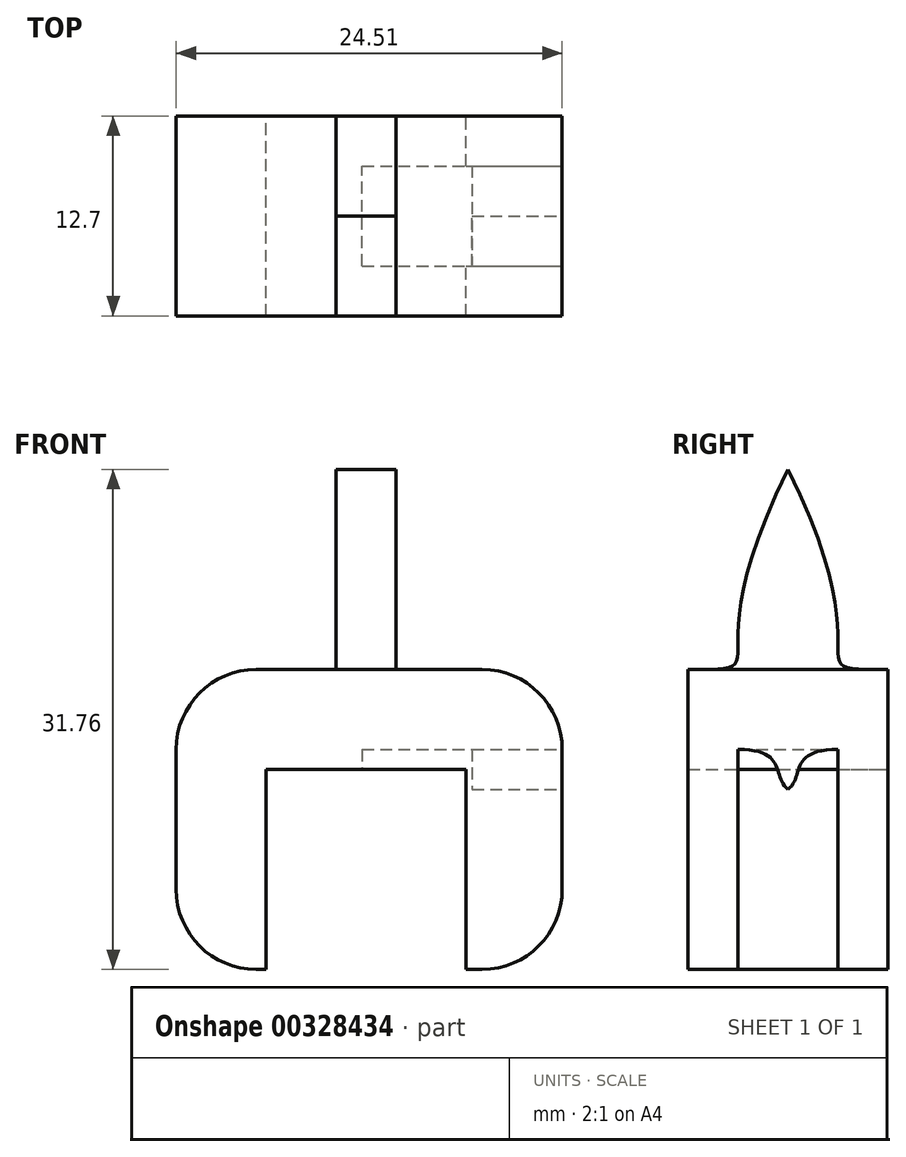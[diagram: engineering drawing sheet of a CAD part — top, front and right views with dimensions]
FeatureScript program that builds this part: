
annotation { "Feature Type Name" : "Feature", "Feature Type Description" : "" }
export const myFeature = defineFeature(function(context is Context, id is Id, definition is map)
    precondition{}
    {
        {
            var Q0;
            Q0=qCreatedBy(makeId("Front.planeOp"),FACE);
            var sketch = newSketch(context, id + "F0", { "sketchPlane" : qUnion([Q0])});
            skLineSegment(sketch, "E0.bottom", {"start": v(-6.35, 3.17) * mm, "end": v(6.35, 3.17) * mm});
            skLineSegment(sketch, "E0.top", {"start": v(-6.35, -3.18) * mm, "end": v(6.35, -3.18) * mm});
            skLineSegment(sketch, "E0.left", {"start": v(-6.35, 3.17) * mm, "end": v(-6.35, -3.18) * mm});
            skLineSegment(sketch, "E0.right", {"start": v(6.35, 3.18) * mm, "end": v(6.35, -3.18) * mm});
            skPoint(sketch, "E0.middle", {"position": v(0, 0) * mm});
            skLineSegment(sketch, "E1.bottom", {"start": v(-6.35, 3.17) * mm, "end": v(-12.05, 3.17) * mm});
            skLineSegment(sketch, "E1.top", {"start": v(-6.35, -15.88) * mm, "end": v(-12.05, -15.88) * mm});
            skLineSegment(sketch, "E1.left", {"start": v(-6.35, 3.17) * mm, "end": v(-6.35, -15.88) * mm});
            skLineSegment(sketch, "E1.right", {"start": v(-12.05, 3.17) * mm, "end": v(-12.05, -15.88) * mm});
            skLineSegment(sketch, "E2.bottom", {"start": v(6.35, 3.17) * mm, "end": v(12.46, 3.17) * mm});
            skLineSegment(sketch, "E2.top", {"start": v(6.35, -15.88) * mm, "end": v(12.46, -15.88) * mm});
            skLineSegment(sketch, "E2.left", {"start": v(6.35, 3.17) * mm, "end": v(6.35, -15.88) * mm});
            skLineSegment(sketch, "E2.right", {"start": v(12.46, 3.17) * mm, "end": v(12.46, -15.88) * mm});
            skSolve(sketch);
        }
        {
            var Q0;
            {var subQ3=sQuery(id+"F0.wireOp",EDGE,"E1.bottom");Q0=makeQuery(id+"F0.imprint","IMPRINT",FACE,{"disambiguationData":[TD([[makeQuery(id+"F0.imprint","IMPRINT",EDGE,{"derivedFrom":subQ3}),1.0]])]});}
            var Q1;
            {var subQ0=sQuery(id+"F0.wireOp",EDGE,"E0.bottom");Q1=makeQuery(id+"F0.imprint","IMPRINT",FACE,{"disambiguationData":[TD([[makeQuery(id+"F0.imprint","IMPRINT",EDGE,{"derivedFrom":subQ0}),-1.0]])]});}
            var Q2;
            {var subQ3=sQuery(id+"F0.wireOp",EDGE,"E2.bottom");Q2=makeQuery(id+"F0.imprint","IMPRINT",FACE,{"disambiguationData":[TD([[makeQuery(id+"F0.imprint","IMPRINT",EDGE,{"derivedFrom":subQ3}),-1.0]])]});}
            extrude(context, id + "F1", {"entities" : qUnion([Q0, Q1, Q2]), "depth" : 12.7 * mm});
        }
        {
            var Q0;
            Q0=makeQuery(id+"F1.opExtrude","SWEPT_EDGE",EDGE,{"disambiguationData":[OSD([sQuery(id+"F0.wireOp",EDGE,"E1.bottom"),sQuery(id+"F0.wireOp",EDGE,"E1.right")])]});
            var Q1;
            Q1=makeQuery(id+"F1.opExtrude","SWEPT_EDGE",EDGE,{"disambiguationData":[OSD([sQuery(id+"F0.wireOp",EDGE,"E2.bottom"),sQuery(id+"F0.wireOp",EDGE,"E2.right")])]});
            var Q2;
            Q2=makeQuery(id+"F1.opExtrude","SWEPT_EDGE",EDGE,{"disambiguationData":[OSD([sQuery(id+"F0.wireOp",EDGE,"E1.top"),sQuery(id+"F0.wireOp",EDGE,"E1.right")])]});
            var Q3;
            Q3=makeQuery(id+"F1.opExtrude","SWEPT_EDGE",EDGE,{"disambiguationData":[OSD([sQuery(id+"F0.wireOp",EDGE,"E2.top"),sQuery(id+"F0.wireOp",EDGE,"E2.right")])]});
            fillet(context, id + "F2", {"entities" : qUnion([Q0, Q1, Q2, Q3]), "radius" : 5.08 * mm, "tangentPropagation" : true, "allowEdgeOverflow" : false});
        }
        {
            var Q0;
            Q0=makeQuery(id+"F1.opExtrude","SWEPT_FACE",FACE,{"disambiguationData":[OSD([sQuery(id+"F0.wireOp",EDGE,"E2.right")])]});
            var sketch = newSketch(context, id + "F3", { "sketchPlane" : qUnion([Q0])});
            skLineSegment(sketch, "E3.bottom", {"start": v(-9.53, -1.9) * mm, "end": v(-3.18, -1.9) * mm});
            skLineSegment(sketch, "E3.top", {"start": v(-9.53, -19.68) * mm, "end": v(-3.18, -19.68) * mm});
            skLineSegment(sketch, "E3.left", {"start": v(-9.53, -1.9) * mm, "end": v(-9.53, -19.68) * mm});
            skLineSegment(sketch, "E3.right", {"start": v(-3.18, -1.9) * mm, "end": v(-3.18, -19.68) * mm});
            skPoint(sketch, "E3.middle", {"position": v(-6.35, -10.8) * mm});
            skSolve(sketch);
        }
        {
            var Q0;
            {var subQ0=sQuery(id+"F3.wireOp",EDGE,"E3.bottom");Q0=makeQuery(id+"F3.imprint","IMPRINT",FACE,{"disambiguationData":[TD([[makeQuery(id+"F3.imprint","IMPRINT",EDGE,{"derivedFrom":subQ0}),1.0]])]});}
            var Q1;
            {var subQ0=sQuery(id+"F3.wireOp",EDGE,"E3.top");Q1=makeQuery(id+"F3.imprint","IMPRINT",FACE,{"disambiguationData":[TD([[makeQuery(id+"F3.imprint","IMPRINT",EDGE,{"derivedFrom":subQ0}),1.0]])]});}
            extrude(context, id + "F4", {"entities" : qUnion([Q0, Q1]), "operationType" : NewBodyOperationType.REMOVE, "oppositeDirection" : true, "depth" : 12.7 * mm});
        }
        {
            var Q0;
            {var subQ0=sQuery(id+"F0.wireOp",EDGE,"E2.right");Q0=makeQuery(id+"F4.boolean.opBoolean","SPLIT",FACE,{"disambiguationData":[TD([makeQuery(id+"F4.opExtrude","SWEPT_FACE",FACE,{"disambiguationData":[OSD([sQuery(id+"F3.wireOp",EDGE,"E3.left")])]})])],"derivedFrom":makeQuery(id+"F1.opExtrude","SWEPT_FACE",FACE,{"disambiguationData":[OSD([subQ0])]})});}
            var sketch = newSketch(context, id + "F5", { "sketchPlane" : qUnion([Q0])});
            skPoint(sketch, "E4", {"position": v(-6.35, -1.9) * mm});
            skLineSegment(sketch, "E5", {"start": v(-3.17, -1.9) * mm, "end": v(-9.53, -1.9) * mm});
            skLineSegment(sketch, "E6", {"start": v(-6.35, -1.9) * mm, "end": v(-6.35, -4.45) * mm});
            skFitSpline(sketch, "E7", {"points": [v(-9.53, -1.9) * mm, v(-6.35, -4.45) * mm], "startDerivative": vector(9.53, 0) * mm, "endDerivative": vector(3.17, -2.54) * mm});
            skFitSpline(sketch, "E8", {"points": [v(-3.17, -1.9) * mm, v(-6.35, -4.45) * mm], "startDerivative": vector(-9.53, 0) * mm, "endDerivative": vector(-3.18, -2.54) * mm});
            skSolve(sketch);
        }
        {
            var Q0;
            {var subQ6=sQuery(id+"F5.wireOp",EDGE,"E6");Q0=makeQuery(id+"F5.imprint","IMPRINT",FACE,{"disambiguationData":[TD([[makeQuery(id+"F5.imprint","IMPRINT",EDGE,{"derivedFrom":subQ6}),-1.0]])]});}
            var Q1;
            {var subQ2=sQuery(id+"F5.wireOp",EDGE,"E6");Q1=makeQuery(id+"F5.imprint","IMPRINT",FACE,{"disambiguationData":[TD([[makeQuery(id+"F5.imprint","IMPRINT",EDGE,{"derivedFrom":subQ2}),1.0]])]});}
            extrude(context, id + "F6", {"entities" : qUnion([Q0, Q1]), "operationType" : NewBodyOperationType.ADD, "oppositeDirection" : true, "depth" : 5.7 * mm});
        }
        {
            var Q0;
            Q0=makeQuery(id+"F1.opExtrude","SWEPT_FACE",FACE,{"disambiguationData":[OSD([sQuery(id+"F0.wireOp",EDGE,"E0.bottom"),sQuery(id+"F0.wireOp",EDGE,"E1.bottom"),sQuery(id+"F0.wireOp",EDGE,"E2.bottom")])]});
            var sketch = newSketch(context, id + "F7", { "sketchPlane" : qUnion([Q0])});
            skLineSegment(sketch, "E9.bottom", {"start": v(-1.9, 0) * mm, "end": v(1.9, 0) * mm});
            skLineSegment(sketch, "E9.top", {"start": v(-1.9, -12.7) * mm, "end": v(1.9, -12.7) * mm});
            skLineSegment(sketch, "E9.left", {"start": v(-1.9, 0) * mm, "end": v(-1.9, -12.7) * mm});
            skLineSegment(sketch, "E9.right", {"start": v(1.9, 0) * mm, "end": v(1.9, -12.7) * mm});
            skSolve(sketch);
        }
        {
            var Q0;
            Q0=makeQuery(id+"F7.imprint","IMPRINT",FACE,{"disambiguationData":[TD([[makeQuery(id+"F7.imprint","IMPRINT",EDGE,{"derivedFrom":sQuery(id+"F7.wireOp",EDGE,"E9.bottom")}),1.0]])]});
            extrude(context, id + "F8", {"entities" : qUnion([Q0]), "operationType" : NewBodyOperationType.ADD, "depth" : 12.7 * mm});
        }
        {
            var Q0;
            Q0=makeQuery(id+"F8.opExtrude","SWEPT_FACE",FACE,{"disambiguationData":[OSD([sQuery(id+"F7.wireOp",EDGE,"E9.right")])]});
            var sketch = newSketch(context, id + "F9", { "sketchPlane" : qUnion([Q0])});
            skPoint(sketch, "E10", {"position": v(-6.35, 15.88) * mm});
            skFitSpline(sketch, "E11", {"points": [v(-12.7, 3.17) * mm, v(-6.35, 15.88) * mm], "startDerivative": vector(19.05, 0) * mm, "endDerivative": vector(19.05, 38.1) * mm});
            skFitSpline(sketch, "E12", {"points": [v(-6.35, 15.88) * mm, v(0, 3.17) * mm], "startDerivative": vector(19.05, -38.1) * mm, "endDerivative": vector(19.05, 0) * mm});
            skSolve(sketch);
        }
        {
            var Q0;
            {var subQ0=sQuery(id+"F9.wireOp",EDGE,"E11");Q0=makeQuery(id+"F9.imprint","IMPRINT",FACE,{"disambiguationData":[TD([[makeQuery(id+"F9.imprint","IMPRINT",EDGE,{"derivedFrom":subQ0}),1.0]])]});}
            var Q1;
            {var subQ0=sQuery(id+"F9.wireOp",EDGE,"E12");Q1=makeQuery(id+"F9.imprint","IMPRINT",FACE,{"disambiguationData":[TD([[makeQuery(id+"F9.imprint","IMPRINT",EDGE,{"derivedFrom":subQ0}),1.0]])]});}
            extrude(context, id + "F10", {"entities" : qUnion([Q0, Q1]), "operationType" : NewBodyOperationType.REMOVE, "oppositeDirection" : true, "depth" : 25.4 * mm});
        }
    });
